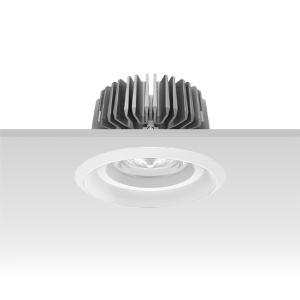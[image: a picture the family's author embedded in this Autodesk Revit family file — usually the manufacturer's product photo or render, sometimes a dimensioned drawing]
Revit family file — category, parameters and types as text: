
# Revit family: 3f_filippi_-_3f_reno_bianco_ampio_3f_filippi_-_30383_-_3f_reno_150_wh_3000-840_dali_wide
name_source: partatom
category: Lighting Fixtures
units: mm (PartAtom-declared; Revit-internal decimal feet)

## family parameters
Cut with Voids When Loaded = No
Host = Face
Light Source = No
Part Type = Normal
Room Calculation Point = No
Round Connector Dimension = Use Diameter
Shared = No

## types (1)
- 3F Filippi - 3F Reno Bianco Ampio (1 x LED, 2757 lm, 28 W, 4000 K)
    Apparent Load = 28 VA
    Approval mark = CE
    CIE Flux Codes = 76 95 100 100 100
    Color Rendering = 80
    Color Temperature = 4000 K
    Control Gear = Electronic transformer
    Default Elevation = 1800 mm
    Description = ILLUMINOTECHNICAL
Luminous efficiency 100% (DLOR 100%, ULOR 0%).
Initial luminous flux of the luminaire 2757 lm.
Direct symmetric wide distribution.
Installation Interdistance Transv.D = 1.54 x hu - Long.D = 1.54 x hu.
Tabular UGR (CIE 117 - 4H-8H; S=0.25H; 70/50/20): RUG 23.4 - 23.4.
Beam angle: 84° - 84°.
Luminous efficacy 98 lm/W.
Lifetime (L90/B10): 30000 h. (tq+25°C)
Lifetime (L85/B10): 50000 h. (tq+25°C)
Lifetime (L70/B10): 80000 h. (tq+25°C)
Sudden decreased luminous flux after 50000 hours: 0% (C0).
Photobiological safety in compliance with IEC/TR 62778: RG0 risk exempt, (IEC 62471).
In compliance with IEC/EN 62722-2-1 - IEC/EN 62717 standards.

SOURCE
Compact LED module 3000/840.
Energy efficiency class (UE 2019/2020 - UE 2019/2015): E.
CIE 13.3 Colour rendering index: CRI >80 (R9 <50%).
IES TM-30 Fidelity Index: Rf = 84 Rg = 95.
CCT nominal colour temperature 4000 K.
Colour initial tolerance (MacAdam): SDCM 3.
Zhaga Book 3 compliant.

MECHANICAL
Passive heat dissipator in die-casting aluminium, oversized, for optimum thermal management of the LED module.
Parabolic element with graduated/concentric rings in white polycarbonate.
Transparent external lens with glossy and satin differentiated surfaces, with a cooling and anti-insect system in methacrylate (PMMA).
Fastening spring clips in stainless steel.
Dimensions: diameter 166 mm, height 107 mm. Weight 1.28 kg.
IP44 protection degree for exposed part, IP20 for recessed part.
Mechanical strength to impacts IK04 (0.5 joule).
Glow-wire test resistance 650°C.

ELECTRICAL
Wiring on a separate unit.
Halogen Free DALI-2 DATI (Parts 251, 252, 253), PUSH-DIM, electronic wiring 230V-50/60Hz, power factor 0.97 at full load, THD <25%, constant output current, SELV, class II, 1 driver, 1 DALI addresse.
Power of the luminaire 28 W.
ENEC - CE.
SAFE FLICKER: PstLM=<1 and SVM=<0.4 (IEC TR 61547-1 and IEC TR 63158), to ensure a more comfortable and safe light.
Luminaire compliant with EN 60598-2-22 for power supply from a centralised emergency system CPSS (Central Power Supply System), not incorporated in the luminaire - high risk areas excluded. The default power and flux are 100% in AC and 100% in DC.
Ambient temperature from 0°C to +25°C.
Temperature class T6 max 85°C.
Relative humidity UR: <85%.

INSTALLATION
Pull-up recessed fitting.
False ceiling carving: 150 mm.
All accessories dedicated to this product are available on the Catalog and on our website www.3F-Filippi.com.

APPLICATIONS
Environments: architectural, commercial, exhibition areas, transit areas, corridors, shops, display windows, service areas.
In false ceilings with narrow voids.

LIGHT MANAGEMENT
Recommended minimum setting: 10%.
The luminaire, equipped with (DALI-2 DATI) driver, can be controlled manually with 3F Easy Dim technology or automatically/manually with wired or wireless DALI/D2D control systems.
The D2D driver guarantees interoperability with other devices with the same certification by making the following information available:
Device Data (Part 251), Energy Report (Part 252), Diagnosis & Maintenance (Part 253).
In electrical systems without a regulation system (manual or automatic) and DALI bus, a suitable jumper must be made on the DA-DA terminals of the appliance.

WARNING
Luminaire designed for disposal/recycling at end-of-life.
Replaceable (LED only) light source by a professional. Replaceable control gear by a professional.
    Height = 0 mm  [stored 0 ft]
    Lamp = 1 x LED
    Lamp Light Flux = 2757 lm
    Lamp Power = 28 W
    Lamp count = 1
    Length = 166 mm
    Lifetime = 50000 h
    Luminous efficacy = 98 lm/W
    Manufacturer = 3F Filippi
    ModVariant = No
    Model = 3F Filippi - 30383 - 3F Reno 150 WH 3000-840 DALI WIDE
    Mounting Place = Ceiling
    Mounting Type = Recessed
    Number of Poles = 1
    OnlyDefault = Yes
    Power Factor = 1
    Product Name = 3F Filippi - 3F Reno Bianco Ampio
    Product group = recessed luminaire
    ProductGroupID = 4
    Protection Class = Protection class II
    Protection Degree = IP 20
    RLX_Detail_Level = 1
    RLX_Emergency_Light_Flux = 0 lm
    RLX_Emergency_Type = 0
    RLX_Emergency_Type_DB = No
    RlxData = <blob elided: 85481 chars, md5=30cdd588>
    Socket = socket
    Standby Power = 0 W
    System Light Flux = 2757 lm
    System Power = 28 W
    Type Comments = Product without accessories
    Type Image = 3ffilippi_3f_reno_150_ampio_wh_3000_4000.jpg
    URL = http://relux.com
    VarID = ---
    Voltage = 0 V
    Weight = 0.00 kg
    Width = 0 mm  [stored 0 ft]

note: [stored X ft] marks values corroborated as IEEE doubles in the binary element streams (Revit-internal decimal feet)

## geometry (parser evidence)
native form markers: Blend x4, Sweep x11
no freeform markers — native parametric forms only
